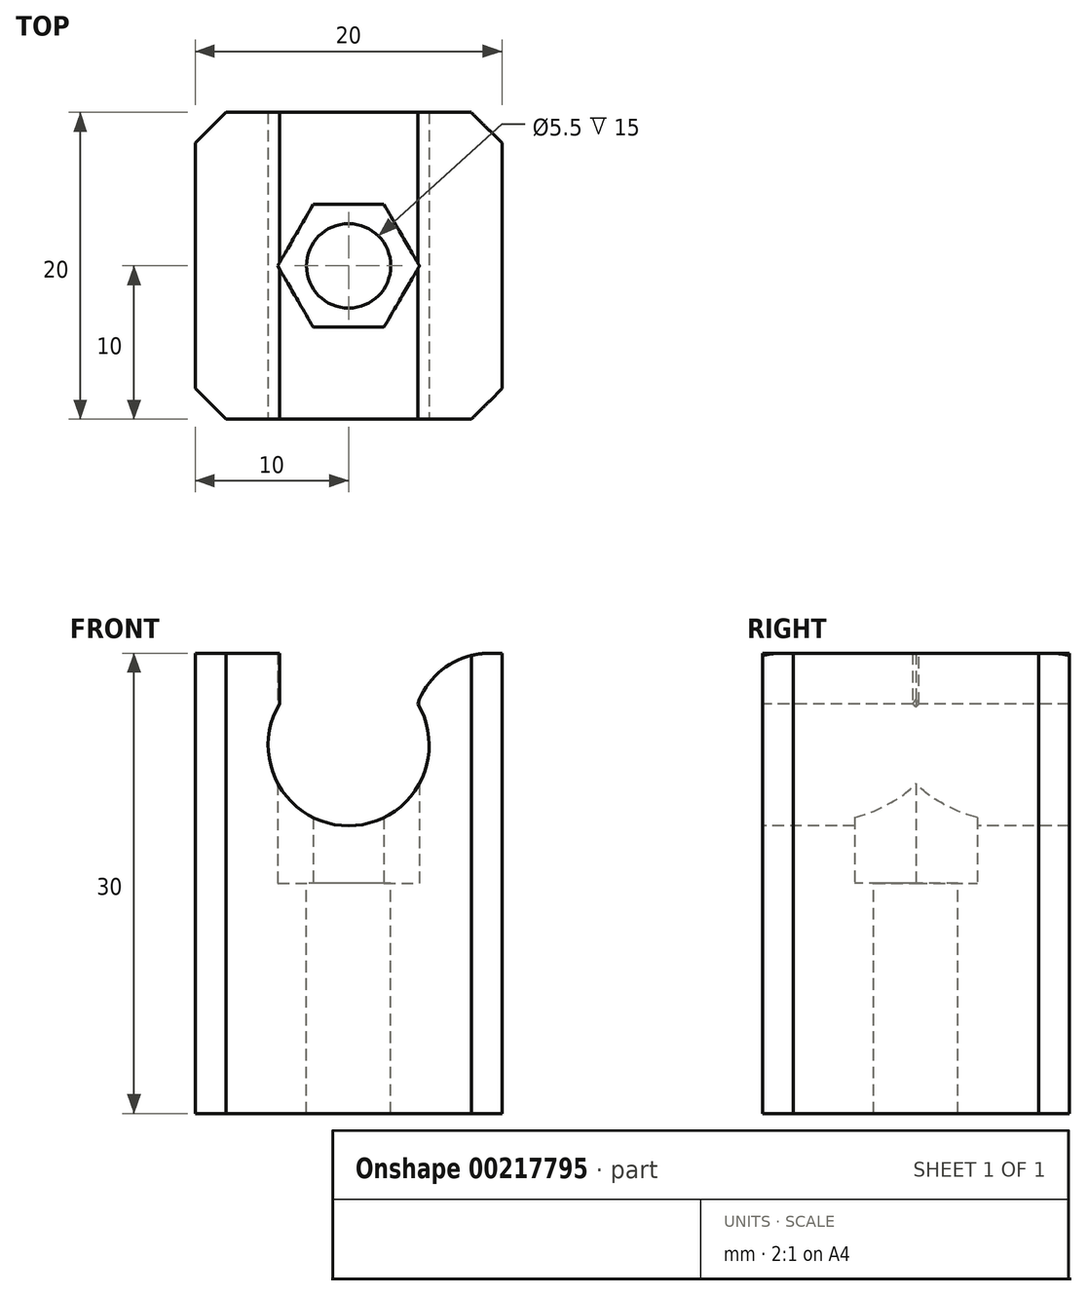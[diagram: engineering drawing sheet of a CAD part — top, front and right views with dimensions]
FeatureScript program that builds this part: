
annotation { "Feature Type Name" : "Feature", "Feature Type Description" : "" }
export const myFeature = defineFeature(function(context is Context, id is Id, definition is map)
    precondition{}
    {
        {
            var Q0;
            Q0=qCreatedBy(makeId("Top.planeOp"),FACE);
            var sketch = newSketch(context, id + "F0", { "sketchPlane" : qUnion([Q0])});
            skLineSegment(sketch, "E0.bottom", {"start": v(-10, 10) * mm, "end": v(10, 10) * mm});
            skLineSegment(sketch, "E0.top", {"start": v(-10, -10) * mm, "end": v(10, -10) * mm});
            skLineSegment(sketch, "E0.left", {"start": v(-10, 10) * mm, "end": v(-10, -10) * mm});
            skLineSegment(sketch, "E0.right", {"start": v(10, 10) * mm, "end": v(10, -10) * mm});
            skPoint(sketch, "E0.middle", {"position": v(0, 0) * mm});
            skCircle(sketch, "E1", {"center": v(0, 0) * mm, "radius": 2.75 * mm});
            skCircle(sketch, "E2.cCircle", {"center": v(0, 0) * mm, "radius": 4 * mm, "construction": true});
            skLineSegment(sketch, "E2.0", {"start": v(-2.3, 4) * mm, "end": v(2.3, 4) * mm});
            skLineSegment(sketch, "E2.1", {"start": v(2.3, 4) * mm, "end": v(4.62, 0) * mm});
            skLineSegment(sketch, "E2.2", {"start": v(4.62, 0) * mm, "end": v(2.3, -4) * mm});
            skLineSegment(sketch, "E2.3", {"start": v(2.3, -4) * mm, "end": v(-2.3, -4) * mm});
            skLineSegment(sketch, "E2.4", {"start": v(-2.3, -4) * mm, "end": v(-4.62, 0) * mm});
            skLineSegment(sketch, "E2.5", {"start": v(-4.62, 0) * mm, "end": v(-2.3, 4) * mm});
            skPoint(sketch, "E2.0.midPoint", {"position": v(0, 4) * mm});
            skSolve(sketch);
        }
        {
            var Q0;
            Q0=makeQuery(id+"F0.imprint","IMPRINT",FACE,{"disambiguationData":[TD([[makeQuery(id+"F0.imprint","IMPRINT",EDGE,{"derivedFrom":sQuery(id+"F0.wireOp",EDGE,"E0.bottom")}),-1.0]])]});
            var Q1;
            Q1=makeQuery(id+"F0.imprint","IMPRINT",FACE,{"disambiguationData":[TD([[makeQuery(id+"F0.imprint","IMPRINT",EDGE,{"derivedFrom":sQuery(id+"F0.wireOp",EDGE,"E1")}),-1.0]])]});
            extrude(context, id + "F1", {"entities" : qUnion([Q0, Q1]), "oppositeDirection" : true, "depth" : 15 * mm});
        }
        {
            var Q0;
            Q0 = qSketchRegion(id + "F0", true);
            extrude(context, id + "F2", {"entities" : qUnion([Q0]), "operationType" : NewBodyOperationType.ADD, "depth" : 15 * mm});
        }
        {
            var Q0;
            {var subQ0=sQuery(id+"F0.wireOp",EDGE,"E0.top");Q0=makeQuery(id+"F2.boolean.opBoolean","MERGE",FACE,{"derivedFrom":[makeQuery(id+"F1.opExtrude","SWEPT_FACE",FACE,{"disambiguationData":[OSD([subQ0])]}),makeQuery(id+"F2.opExtrude","SWEPT_FACE",FACE,{"disambiguationData":[OSD([subQ0])]})]});}
            var sketch = newSketch(context, id + "F3", { "sketchPlane" : qUnion([Q0])});
            skCircle(sketch, "E3", {"center": v(0, 9) * mm, "radius": 5.25 * mm});
            skLineSegment(sketch, "E4", {"start": v(-4.5, 15) * mm, "end": v(-4.5, 11.7) * mm});
            skLineSegment(sketch, "E5", {"start": v(4.5, 15) * mm, "end": v(4.5, 11.7) * mm});
            skSolve(sketch);
        }
        {
            var Q0;
            {var subQ0=sQuery(id+"F3.wireOp",EDGE,"E3");var subQ1=makeQuery(id+"F3.imprint","INTERSECT",VERTEX,{"derivedFrom":[subQ0,sQuery(id+"F3.wireOp",EDGE,"E4")]});Q0=makeQuery(id+"F3.imprint","IMPRINT",FACE,{"disambiguationData":[TD([[makeQuery(id+"F3.imprint","IMPRINT",EDGE,{"disambiguationData":[TD([[subQ1,1.0]])],"derivedFrom":subQ0}),1.0]])]});}
            var Q1;
            {var subQ0=sQuery(id+"F3.wireOp",EDGE,"E4");Q1=makeQuery(id+"F3.imprint","IMPRINT",FACE,{"disambiguationData":[TD([[makeQuery(id+"F3.imprint","IMPRINT",EDGE,{"derivedFrom":subQ0}),1.0]])]});}
            var Q2;
            {var subQ0=sQuery(id+"F0.wireOp",EDGE,"E0.bottom");Q2=makeQuery(id+"F2.boolean.opBoolean","MERGE",FACE,{"derivedFrom":[makeQuery(id+"F1.opExtrude","SWEPT_FACE",FACE,{"disambiguationData":[OSD([subQ0])]}),makeQuery(id+"F2.opExtrude","SWEPT_FACE",FACE,{"disambiguationData":[OSD([subQ0])]})]});}
            extrude(context, id + "F4", {"entities" : qUnion([Q0, Q1]), "operationType" : NewBodyOperationType.REMOVE, "endBound" : BoundingType.UP_TO_SURFACE, "oppositeDirection" : true, "endBoundEntityFace" : qUnion([Q2]), "depth" : 25 * mm});
        }
        {
            var Q0;
            {var subQ1=sQuery(id+"F0.wireOp",EDGE,"E0.top");var subQ2=sQuery(id+"F3.wireOp",EDGE,"E4");Q0=makeQuery(id+"F4.boolean.opBoolean","COPY",EDGE,{"disambiguationData":[TD([makeQuery(id+"F1.opExtrude","SWEPT_FACE",FACE,{"disambiguationData":[OSD([subQ1])]})])],"derivedFrom":makeQuery(id+"F4.opExtrude","SWEPT_EDGE",EDGE,{"disambiguationData":[OSD([subQ1,subQ2])]})});}
            var Q1;
            {var subQ1=sQuery(id+"F0.wireOp",EDGE,"E0.top");var subQ2=sQuery(id+"F3.wireOp",EDGE,"E5");Q1=makeQuery(id+"F4.boolean.opBoolean","COPY",EDGE,{"disambiguationData":[TD([makeQuery(id+"F1.opExtrude","SWEPT_FACE",FACE,{"disambiguationData":[OSD([subQ1])]})])],"derivedFrom":makeQuery(id+"F4.opExtrude","SWEPT_EDGE",EDGE,{"disambiguationData":[OSD([subQ1,subQ2])]})});}
            fillet(context, id + "F5", {"entities" : qUnion([Q0, Q1]), "radius" : 5 * mm, "tangentPropagation" : true, "allowEdgeOverflow" : false});
        }
        {
            var Q0;
            {var subQ0=sQuery(id+"F0.wireOp",EDGE,"E0.left");var subQ1=sQuery(id+"F0.wireOp",EDGE,"E0.top");Q0=makeQuery(id+"F2.boolean.opBoolean","MERGE",EDGE,{"derivedFrom":[makeQuery(id+"F1.opExtrude","SWEPT_EDGE",EDGE,{"disambiguationData":[OSD([subQ1,subQ0])]}),makeQuery(id+"F2.opExtrude","SWEPT_EDGE",EDGE,{"disambiguationData":[OSD([subQ1,subQ0])]})]});}
            var Q1;
            {var subQ0=sQuery(id+"F0.wireOp",EDGE,"E0.right");var subQ1=sQuery(id+"F0.wireOp",EDGE,"E0.top");Q1=makeQuery(id+"F2.boolean.opBoolean","MERGE",EDGE,{"derivedFrom":[makeQuery(id+"F1.opExtrude","SWEPT_EDGE",EDGE,{"disambiguationData":[OSD([subQ1,subQ0])]}),makeQuery(id+"F2.opExtrude","SWEPT_EDGE",EDGE,{"disambiguationData":[OSD([subQ1,subQ0])]})]});}
            var Q2;
            {var subQ0=sQuery(id+"F0.wireOp",EDGE,"E0.left");var subQ1=sQuery(id+"F0.wireOp",EDGE,"E0.bottom");Q2=makeQuery(id+"F2.boolean.opBoolean","MERGE",EDGE,{"derivedFrom":[makeQuery(id+"F1.opExtrude","SWEPT_EDGE",EDGE,{"disambiguationData":[OSD([subQ1,subQ0])]}),makeQuery(id+"F2.opExtrude","SWEPT_EDGE",EDGE,{"disambiguationData":[OSD([subQ1,subQ0])]})]});}
            var Q3;
            {var subQ0=sQuery(id+"F0.wireOp",EDGE,"E0.right");var subQ1=sQuery(id+"F0.wireOp",EDGE,"E0.bottom");Q3=makeQuery(id+"F2.boolean.opBoolean","MERGE",EDGE,{"derivedFrom":[makeQuery(id+"F1.opExtrude","SWEPT_EDGE",EDGE,{"disambiguationData":[OSD([subQ1,subQ0])]}),makeQuery(id+"F2.opExtrude","SWEPT_EDGE",EDGE,{"disambiguationData":[OSD([subQ1,subQ0])]})]});}
            chamfer(context, id + "F6", {"entities" : qUnion([Q0, Q1, Q2, Q3]), "width" : 2 * mm, "tangentPropagation" : true});
        }
    });
